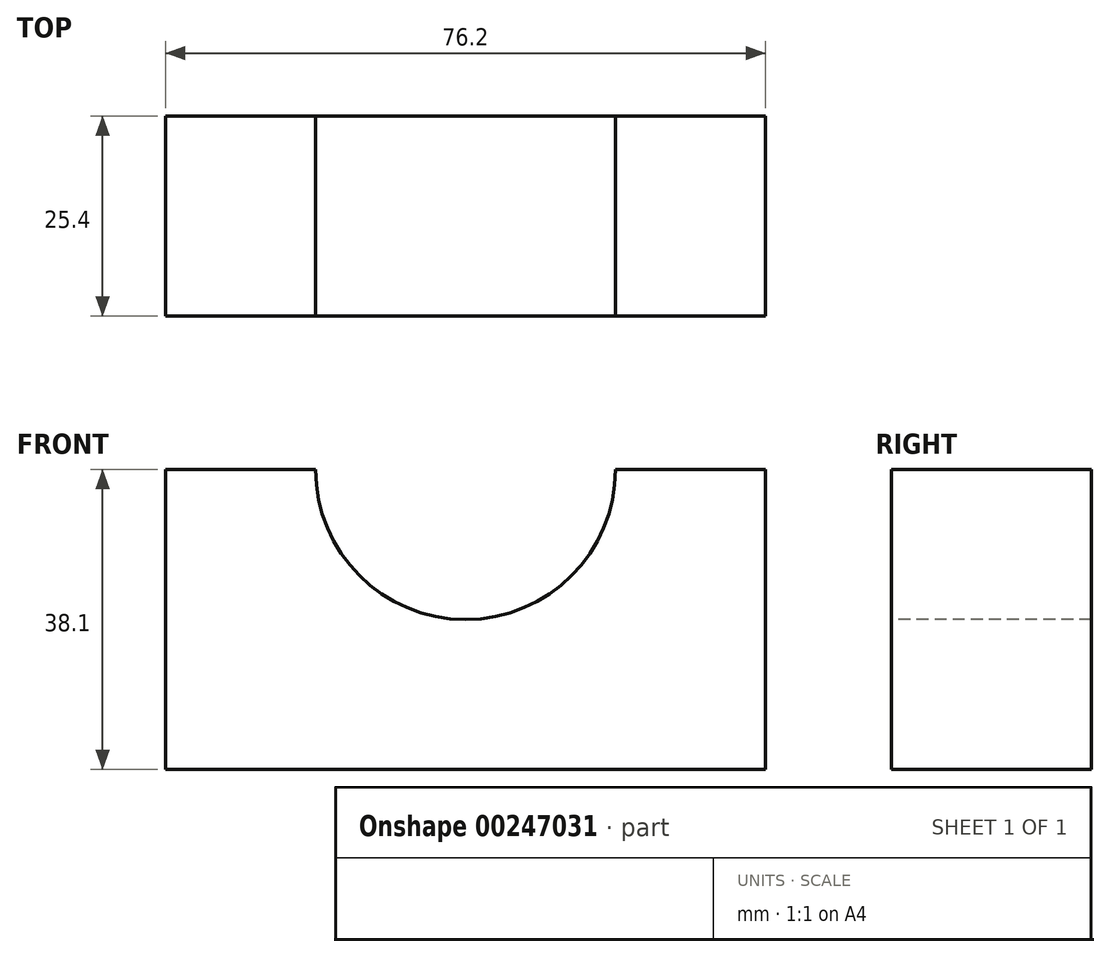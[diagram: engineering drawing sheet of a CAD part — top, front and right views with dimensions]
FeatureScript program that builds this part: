
annotation { "Feature Type Name" : "Feature", "Feature Type Description" : "" }
export const myFeature = defineFeature(function(context is Context, id is Id, definition is map)
    precondition{}
    {
        {
            var Q0;
            Q0=qCreatedBy(makeId("Top.planeOp"),FACE);
            var sketch = newSketch(context, id + "F0", { "sketchPlane" : qUnion([Q0])});
            skLineSegment(sketch, "E0", {"start": v(-38.1, 0) * mm, "end": v(-38.1, 12.7) * mm});
            skLineSegment(sketch, "E1", {"start": v(-38.1, 12.7) * mm, "end": v(0, 12.7) * mm});
            skLineSegment(sketch, "E2", {"start": v(0, 12.7) * mm, "end": v(38.1, 12.7) * mm});
            skLineSegment(sketch, "E3", {"start": v(38.1, 12.7) * mm, "end": v(38.1, 0) * mm});
            skLineSegment(sketch, "E4", {"start": v(0, -12.7) * mm, "end": v(38.1, -12.7) * mm});
            skLineSegment(sketch, "E5", {"start": v(38.1, -12.7) * mm, "end": v(38.1, 0) * mm});
            skLineSegment(sketch, "E6", {"start": v(0, -12.7) * mm, "end": v(-38.1, -12.7) * mm});
            skLineSegment(sketch, "E7", {"start": v(-38.1, -12.7) * mm, "end": v(-38.1, 0) * mm});
            skPoint(sketch, "E8.end.orphan", {"position": v(0, 0) * mm});
            skSolve(sketch);
        }
        {
            var Q0;
            Q0=makeQuery(id+"F0.imprint","IMPRINT",FACE,{"disambiguationData":[TD([[makeQuery(id+"F0.imprint","IMPRINT",EDGE,{"derivedFrom":sQuery(id+"F0.wireOp",EDGE,"E0")}),-1.0]])]});
            extrude(context, id + "F1", {"entities" : qUnion([Q0]), "depth" : 38.1 * mm});
        }
        {
            var Q0;
            Q0=makeQuery(id+"F1.opExtrude","SWEPT_FACE",FACE,{"disambiguationData":[OSD([sQuery(id+"F0.wireOp",EDGE,"E4"),sQuery(id+"F0.wireOp",EDGE,"E6")])]});
            var sketch = newSketch(context, id + "F2", { "sketchPlane" : qUnion([Q0])});
            skArc(sketch, "E9", {"start": v(-19.05, 38.1) * mm, "mid": v(0, 19.05) * mm, "end": v(19.05, 38.1) * mm});
            skLineSegment(sketch, "E10", {"start": v(-38.1, 38.1) * mm, "end": v(38.1, 38.1) * mm});
            skSolve(sketch);
        }
        {
            var Q0;
            {var subQ0=sQuery(id+"F2.wireOp",EDGE,"E9");Q0=makeQuery(id+"F2.imprint","IMPRINT",FACE,{"disambiguationData":[TD([[makeQuery(id+"F2.imprint","IMPRINT",EDGE,{"derivedFrom":subQ0}),1.0]])]});}
            extrude(context, id + "F3", {"entities" : qUnion([Q0]), "operationType" : NewBodyOperationType.REMOVE, "oppositeDirection" : true, "depth" : 25.4 * mm});
        }
    });
